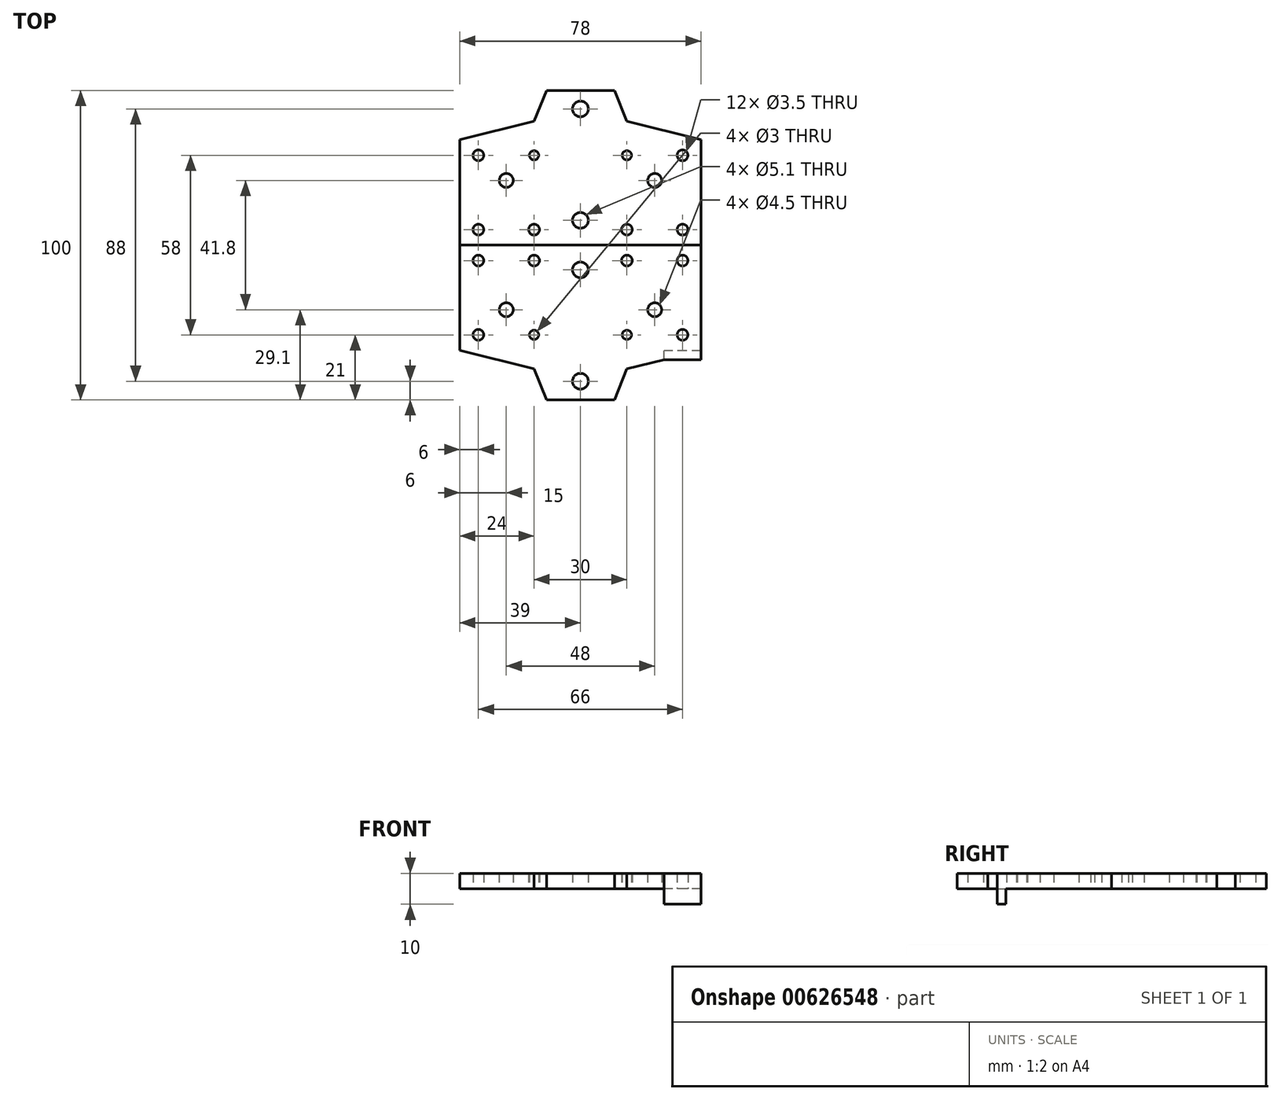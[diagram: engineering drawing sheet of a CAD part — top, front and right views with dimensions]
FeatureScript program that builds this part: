
annotation { "Feature Type Name" : "Feature", "Feature Type Description" : "" }
export const myFeature = defineFeature(function(context is Context, id is Id, definition is map)
    precondition{}
    {
        {
            var Q0;
            Q0=qCreatedBy(makeId("Top.planeOp"),FACE);
            var sketch = newSketch(context, id + "F0", { "sketchPlane" : qUnion([Q0])});
            skLineSegment(sketch, "E0.bottom", {"start": v(39, -17) * mm, "end": v(-39, -17) * mm});
            skLineSegment(sketch, "E0.top", {"start": v(39, 17) * mm, "end": v(-39, 17) * mm});
            skLineSegment(sketch, "E0.left", {"start": v(39, -17) * mm, "end": v(39, 17) * mm});
            skLineSegment(sketch, "E0.right", {"start": v(-39, -17) * mm, "end": v(-39, 17) * mm});
            skPoint(sketch, "E0.middle", {"position": v(0, 0) * mm});
            skLineSegment(sketch, "E1", {"start": v(-11, 33) * mm, "end": v(11, 33) * mm});
            skLineSegment(sketch, "E2", {"start": v(0, -17) * mm, "end": v(0, 41.6) * mm, "construction": true});
            skLineSegment(sketch, "E3", {"start": v(33, -17) * mm, "end": v(33, 17) * mm, "construction": true});
            skLineSegment(sketch, "E4", {"start": v(-33, -17) * mm, "end": v(-33, 17) * mm, "construction": true});
            skLineSegment(sketch, "E5", {"start": v(-39, -12) * mm, "end": v(39, -12) * mm, "construction": true});
            skLineSegment(sketch, "E6", {"start": v(-39, 12) * mm, "end": v(39, 12) * mm, "construction": true});
            skCircle(sketch, "E7", {"center": v(33, 12) * mm, "radius": 1.75 * mm});
            skCircle(sketch, "E8", {"center": v(33, -12) * mm, "radius": 1.75 * mm});
            skCircle(sketch, "E9", {"center": v(-33, -12) * mm, "radius": 1.75 * mm});
            skCircle(sketch, "E10", {"center": v(-33, 12) * mm, "radius": 1.75 * mm});
            skCircle(sketch, "E11", {"center": v(-15, 12) * mm, "radius": 1.5 * mm});
            skCircle(sketch, "E12", {"center": v(-15, -12) * mm, "radius": 1.75 * mm});
            skCircle(sketch, "E13", {"center": v(15, 12) * mm, "radius": 1.5 * mm});
            skCircle(sketch, "E14", {"center": v(15, -12) * mm, "radius": 1.75 * mm});
            skCircle(sketch, "E15", {"center": v(0, 27) * mm, "radius": 2.55 * mm});
            skCircle(sketch, "E16", {"center": v(0, -9) * mm, "radius": 2.55 * mm});
            skCircle(sketch, "E17", {"center": v(24, 3.9) * mm, "radius": 2.25 * mm});
            skCircle(sketch, "E18", {"center": v(-24, 3.9) * mm, "radius": 2.25 * mm});
            skLineSegment(sketch, "E19", {"start": v(-11, 33) * mm, "end": v(-15, 23) * mm});
            skLineSegment(sketch, "E20", {"start": v(-15, 23) * mm, "end": v(-39, 17) * mm});
            skLineSegment(sketch, "E21", {"start": v(11, 33) * mm, "end": v(15, 23) * mm});
            skLineSegment(sketch, "E22", {"start": v(15, 23) * mm, "end": v(39, 17) * mm});
            skSolve(sketch);
        }
        {
            var Q0;
            Q0=makeQuery(id+"F0.imprint","IMPRINT",FACE,{"disambiguationData":[TD([[makeQuery(id+"F0.imprint","IMPRINT",EDGE,{"derivedFrom":sQuery(id+"F0.wireOp",EDGE,"E0.bottom")}),-1.0]])]});
            var Q1;
            Q1=makeQuery(id+"F0.imprint","IMPRINT",FACE,{"disambiguationData":[TD([[makeQuery(id+"F0.imprint","IMPRINT",EDGE,{"derivedFrom":sQuery(id+"F0.wireOp",EDGE,"E0.top")}),-1.0]])]});
            extrude(context, id + "F1", {"entities" : qUnion([Q0, Q1]), "depth" : 5 * mm, "offsetDistance" : 25 * mm});
        }
        {
            var Q0;
            Q0=makeQuery(id+"F1.opExtrude","SWEPT_BODY",BODY,{"disambiguationData":[OSD([sQuery(id+"F0.wireOp",EDGE,"E0.bottom"),sQuery(id+"F0.wireOp",EDGE,"E0.left"),sQuery(id+"F0.wireOp",EDGE,"E0.right"),sQuery(id+"F0.wireOp",EDGE,"E1"),sQuery(id+"F0.wireOp",EDGE,"E7"),sQuery(id+"F0.wireOp",EDGE,"E8"),sQuery(id+"F0.wireOp",EDGE,"E9"),sQuery(id+"F0.wireOp",EDGE,"E10"),sQuery(id+"F0.wireOp",EDGE,"E11"),sQuery(id+"F0.wireOp",EDGE,"E12"),sQuery(id+"F0.wireOp",EDGE,"E13"),sQuery(id+"F0.wireOp",EDGE,"E14"),sQuery(id+"F0.wireOp",EDGE,"E15"),sQuery(id+"F0.wireOp",EDGE,"E16"),sQuery(id+"F0.wireOp",EDGE,"E17"),sQuery(id+"F0.wireOp",EDGE,"E18"),sQuery(id+"F0.wireOp",EDGE,"E19"),sQuery(id+"F0.wireOp",EDGE,"E20"),sQuery(id+"F0.wireOp",EDGE,"E21"),sQuery(id+"F0.wireOp",EDGE,"E22")])]});
            var Q1;
            Q1=makeQuery(id+"F1.opExtrude","SWEPT_FACE",FACE,{"disambiguationData":[OSD([sQuery(id+"F0.wireOp",EDGE,"E0.bottom")])]});
            mirror(context, id + "F2", {"entities" : qUnion([Q0]), "mirrorPlane" : qUnion([Q1])});
        }
        {
            var Q0;
            Q0=makeQuery(id+"F2.opPattern","COPY",FACE,{"derivedFrom":makeQuery(id+"F1.opExtrude","CAP_FACE",FACE,{"disambiguationData":[OSD([sQuery(id+"F0.wireOp",EDGE,"E0.bottom"),sQuery(id+"F0.wireOp",EDGE,"E0.left"),sQuery(id+"F0.wireOp",EDGE,"E0.right"),sQuery(id+"F0.wireOp",EDGE,"E1"),sQuery(id+"F0.wireOp",EDGE,"E7"),sQuery(id+"F0.wireOp",EDGE,"E8"),sQuery(id+"F0.wireOp",EDGE,"E9"),sQuery(id+"F0.wireOp",EDGE,"E10"),sQuery(id+"F0.wireOp",EDGE,"E11"),sQuery(id+"F0.wireOp",EDGE,"E12"),sQuery(id+"F0.wireOp",EDGE,"E13"),sQuery(id+"F0.wireOp",EDGE,"E14"),sQuery(id+"F0.wireOp",EDGE,"E15"),sQuery(id+"F0.wireOp",EDGE,"E16"),sQuery(id+"F0.wireOp",EDGE,"E17"),sQuery(id+"F0.wireOp",EDGE,"E18"),sQuery(id+"F0.wireOp",EDGE,"E19"),sQuery(id+"F0.wireOp",EDGE,"E20"),sQuery(id+"F0.wireOp",EDGE,"E21"),sQuery(id+"F0.wireOp",EDGE,"E22")])],"isStart":false}),"instanceName":"1"});
            var sketch = newSketch(context, id + "F3", { "sketchPlane" : qUnion([Q0])});
            skLineSegment(sketch, "E23", {"start": v(27, -54) * mm, "end": v(39, -54) * mm});
            skLineSegment(sketch, "E24", {"start": v(39, -54) * mm, "end": v(39, -51) * mm});
            skSolve(sketch);
        }
        {
            var Q0;
            {var subQ0=sQuery(id+"F3.wireOp",EDGE,"E23");Q0=makeQuery(id+"F3.imprint","IMPRINT",FACE,{"disambiguationData":[TD([[makeQuery(id+"F3.imprint","IMPRINT",EDGE,{"derivedFrom":subQ0}),1.0]])]});}
            var Q1;
            Q1=makeQuery(id+"F2.opPattern","COPY",FACE,{"derivedFrom":makeQuery(id+"F1.opExtrude","CAP_FACE",FACE,{"disambiguationData":[OSD([sQuery(id+"F0.wireOp",EDGE,"E0.bottom"),sQuery(id+"F0.wireOp",EDGE,"E0.left"),sQuery(id+"F0.wireOp",EDGE,"E0.right"),sQuery(id+"F0.wireOp",EDGE,"E1"),sQuery(id+"F0.wireOp",EDGE,"E7"),sQuery(id+"F0.wireOp",EDGE,"E8"),sQuery(id+"F0.wireOp",EDGE,"E9"),sQuery(id+"F0.wireOp",EDGE,"E10"),sQuery(id+"F0.wireOp",EDGE,"E11"),sQuery(id+"F0.wireOp",EDGE,"E12"),sQuery(id+"F0.wireOp",EDGE,"E13"),sQuery(id+"F0.wireOp",EDGE,"E14"),sQuery(id+"F0.wireOp",EDGE,"E15"),sQuery(id+"F0.wireOp",EDGE,"E16"),sQuery(id+"F0.wireOp",EDGE,"E17"),sQuery(id+"F0.wireOp",EDGE,"E18"),sQuery(id+"F0.wireOp",EDGE,"E19"),sQuery(id+"F0.wireOp",EDGE,"E20"),sQuery(id+"F0.wireOp",EDGE,"E21"),sQuery(id+"F0.wireOp",EDGE,"E22")])],"isStart":true}),"instanceName":"1"});
            extrude(context, id + "F4", {"entities" : qUnion([Q0]), "operationType" : NewBodyOperationType.ADD, "endBound" : BoundingType.UP_TO_SURFACE, "oppositeDirection" : true, "depth" : 25 * mm, "endBoundEntityFace" : qUnion([Q1]), "offsetDistance" : 25 * mm});
        }
        {
            var Q0;
            {var subQ0=sQuery(id+"F0.wireOp",EDGE,"E22");var subQ1=sQuery(id+"F0.wireOp",EDGE,"E21");var subQ2=sQuery(id+"F0.wireOp",EDGE,"E20");var subQ3=sQuery(id+"F0.wireOp",EDGE,"E19");var subQ4=sQuery(id+"F0.wireOp",EDGE,"E18");var subQ5=sQuery(id+"F0.wireOp",EDGE,"E17");var subQ6=sQuery(id+"F0.wireOp",EDGE,"E16");var subQ7=sQuery(id+"F0.wireOp",EDGE,"E15");var subQ8=sQuery(id+"F0.wireOp",EDGE,"E14");var subQ9=sQuery(id+"F0.wireOp",EDGE,"E13");var subQ10=sQuery(id+"F0.wireOp",EDGE,"E12");var subQ11=sQuery(id+"F0.wireOp",EDGE,"E11");var subQ12=sQuery(id+"F0.wireOp",EDGE,"E10");var subQ13=sQuery(id+"F0.wireOp",EDGE,"E9");var subQ14=sQuery(id+"F0.wireOp",EDGE,"E8");var subQ15=sQuery(id+"F0.wireOp",EDGE,"E7");var subQ16=sQuery(id+"F0.wireOp",EDGE,"E1");var subQ17=sQuery(id+"F0.wireOp",EDGE,"E0.right");var subQ18=sQuery(id+"F0.wireOp",EDGE,"E0.left");var subQ19=sQuery(id+"F0.wireOp",EDGE,"E0.bottom");Q0=makeQuery(id+"F4.boolean.opBoolean","MERGE",FACE,{"derivedFrom":[makeQuery(id+"F2.opPattern","COPY",FACE,{"derivedFrom":makeQuery(id+"F1.opExtrude","CAP_FACE",FACE,{"disambiguationData":[OSD([subQ19,subQ18,subQ17,subQ16,subQ15,subQ14,subQ13,subQ12,subQ11,subQ10,subQ9,subQ8,subQ7,subQ6,subQ5,subQ4,subQ3,subQ2,subQ1,subQ0])],"isStart":true}),"instanceName":"1"}),makeQuery(id+"F4.opExtrude","CAP_FACE",FACE,{"disambiguationData":[OSD([subQ19,subQ18,subQ17,subQ16,subQ15,subQ14,subQ13,subQ12,subQ11,subQ10,subQ9,subQ8,subQ7,subQ6,subQ5,subQ4,subQ3,subQ2,subQ1,subQ0])],"isStart":false})]});}
            var sketch = newSketch(context, id + "F5", { "sketchPlane" : qUnion([Q0])});
            skLineSegment(sketch, "E25.bottom", {"start": v(39, 54) * mm, "end": v(27, 54) * mm});
            skLineSegment(sketch, "E25.top", {"start": v(39, 51.2) * mm, "end": v(27, 51.2) * mm});
            skLineSegment(sketch, "E25.left", {"start": v(39, 54) * mm, "end": v(39, 51.2) * mm});
            skLineSegment(sketch, "E25.right", {"start": v(27, 54) * mm, "end": v(27, 51.2) * mm});
            skSolve(sketch);
        }
        {
            var Q0;
            Q0=makeQuery(id+"F5.imprint","IMPRINT",FACE,{"disambiguationData":[TD([[makeQuery(id+"F5.imprint","IMPRINT",EDGE,{"derivedFrom":sQuery(id+"F5.wireOp",EDGE,"E25.bottom")}),1.0]])]});
            extrude(context, id + "F6", {"entities" : qUnion([Q0]), "operationType" : NewBodyOperationType.ADD, "depth" : 5 * mm, "offsetDistance" : 25 * mm});
        }
    });
